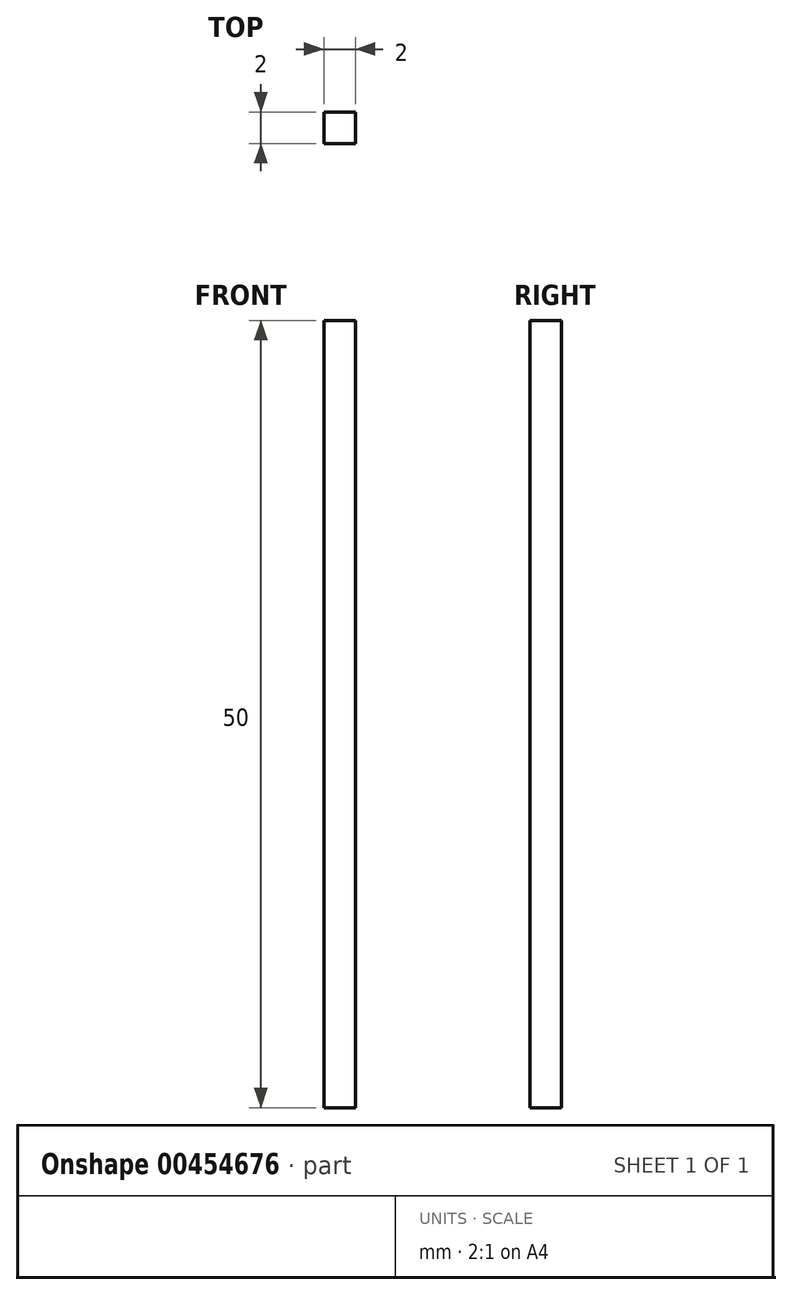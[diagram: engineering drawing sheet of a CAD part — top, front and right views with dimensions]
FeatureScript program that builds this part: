
annotation { "Feature Type Name" : "Feature", "Feature Type Description" : "" }
export const myFeature = defineFeature(function(context is Context, id is Id, definition is map)
    precondition{}
    {
        {
            var Q0;
            Q0=qCreatedBy(makeId("Front.planeOp"),FACE);
            var sketch = newSketch(context, id + "F0", { "sketchPlane" : qUnion([Q0])});
            skLineSegment(sketch, "E0.bottom", {"start": v(0, 0) * mm, "end": v(2, 0) * mm});
            skLineSegment(sketch, "E0.top", {"start": v(0, 50) * mm, "end": v(2, 50) * mm});
            skLineSegment(sketch, "E0.left", {"start": v(0, 0) * mm, "end": v(0, 50) * mm});
            skLineSegment(sketch, "E0.right", {"start": v(2, 0) * mm, "end": v(2, 50) * mm});
            skSolve(sketch);
        }
        {
            var Q0;
            Q0 = qSketchRegion(id + "F0", true);
            extrude(context, id + "F1", {"entities" : qUnion([Q0]), "depth" : 2 * mm, "offsetDistance" : 25 * mm});
        }
    });
